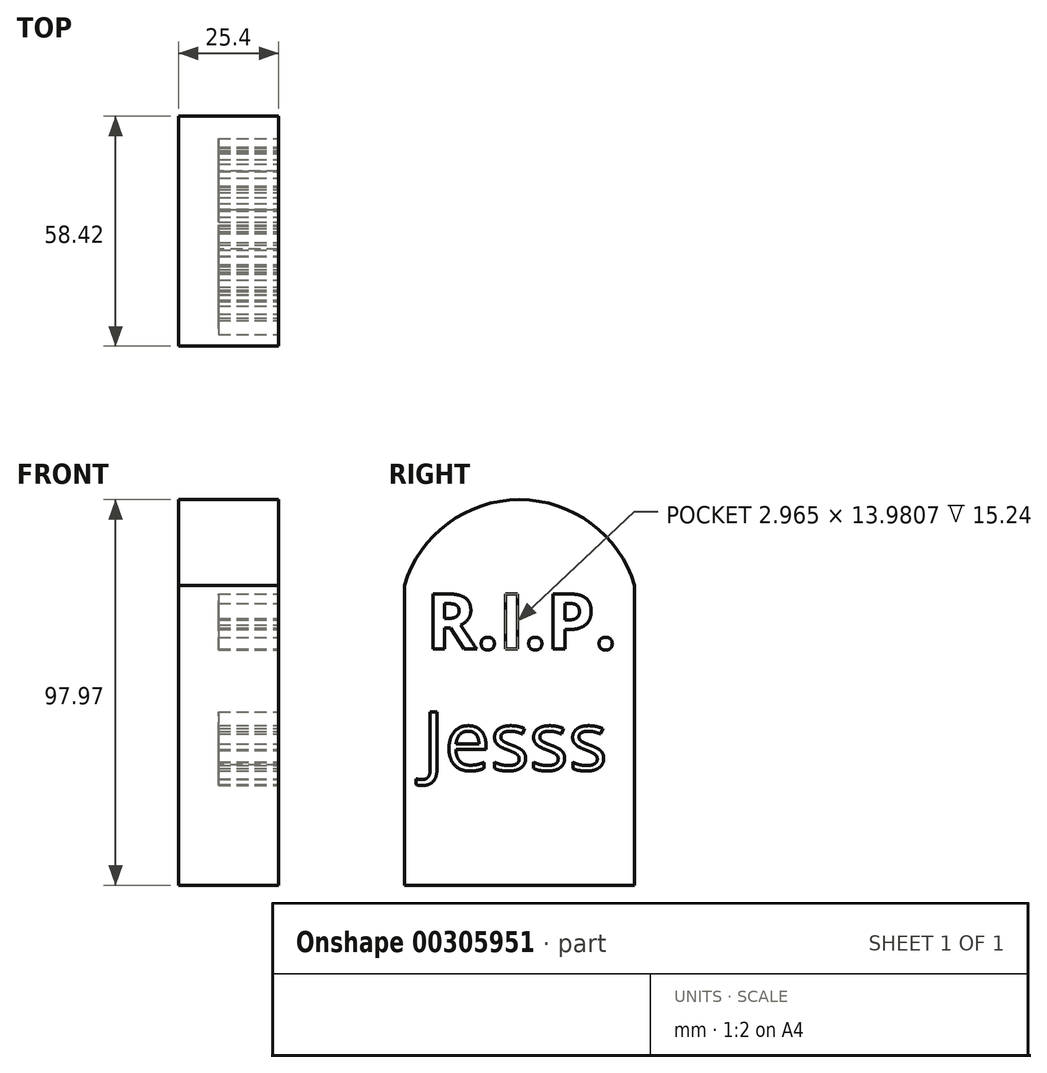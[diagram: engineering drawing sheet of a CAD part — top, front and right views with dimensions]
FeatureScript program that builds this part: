
annotation { "Feature Type Name" : "Feature", "Feature Type Description" : "" }
export const myFeature = defineFeature(function(context is Context, id is Id, definition is map)
    precondition{}
    {
        {
            var Q0;
            Q0=qCreatedBy(makeId("Right.planeOp"),FACE);
            var sketch = newSketch(context, id + "F0", { "sketchPlane" : qUnion([Q0])});
            skLineSegment(sketch, "E0.bottom", {"start": v(-17.8, -44.2) * mm, "end": v(40.62, -44.2) * mm});
            skLineSegment(sketch, "E0.top", {"start": v(-17.8, 32) * mm, "end": v(40.62, 32) * mm});
            skLineSegment(sketch, "E0.left", {"start": v(-17.8, -44.2) * mm, "end": v(-17.8, 32) * mm});
            skLineSegment(sketch, "E0.right", {"start": v(40.62, -44.2) * mm, "end": v(40.62, 32) * mm});
            skArc(sketch, "E1", {"start": v(40.62, 32) * mm, "mid": v(11.4, 53.78) * mm, "end": v(-17.8, 32) * mm});
            skSolve(sketch);
        }
        {
            var Q0;
            Q0=makeQuery(id+"F0.imprint","IMPRINT",FACE,{"disambiguationData":[TD([[makeQuery(id+"F0.imprint","IMPRINT",EDGE,{"derivedFrom":sQuery(id+"F0.wireOp",EDGE,"E0.bottom")}),1.0]])]});
            extrude(context, id + "F1", {"entities" : qUnion([Q0]), "depth" : 25.4 * mm});
        }
        {
            var Q0;
            Q0 = qSketchRegion(id + "F0", true);
            extrude(context, id + "F2", {"entities" : qUnion([Q0]), "operationType" : NewBodyOperationType.ADD, "depth" : 25.4 * mm});
        }
        {
            var Q0;
            {var subQ0=sQuery(id+"F0.wireOp",EDGE,"E0.right");var subQ1=sQuery(id+"F0.wireOp",EDGE,"E0.left");var subQ2=sQuery(id+"F0.wireOp",EDGE,"E0.bottom");Q0=makeQuery(id+"F2.boolean.opBoolean","MERGE",FACE,{"derivedFrom":[makeQuery(id+"F1.opExtrude","CAP_FACE",FACE,{"disambiguationData":[OSD([subQ2,sQuery(id+"F0.wireOp",EDGE,"E0.top"),subQ1,subQ0])],"isStart":false}),makeQuery(id+"F2.opExtrude","CAP_FACE",FACE,{"disambiguationData":[OSD([subQ2,subQ1,subQ0,sQuery(id+"F0.wireOp",EDGE,"E1")])],"isStart":false})]});}
            var sketch = newSketch(context, id + "F3", { "sketchPlane" : qUnion([Q0])});
            skText(sketch, "E2", { "text": "Jesss", "fontName": "OpenSans-Regular.ttf"});
            const initialGuessF3  = {"E2": [-0.01323, -0.01497, 1, 0, 0.01497]};
            skSetInitialGuess(sketch, initialGuessF3);
            skSolve(sketch);
        }
        {
            var Q0;
            Q0 = qSketchRegion(id + "F3", true);
            extrude(context, id + "F4", {"entities" : qUnion([Q0]), "operationType" : NewBodyOperationType.REMOVE, "oppositeDirection" : true, "depth" : 15.24 * mm});
        }
        {
            var Q0;
            {var subQ0=sQuery(id+"F0.wireOp",EDGE,"E0.right");var subQ1=sQuery(id+"F0.wireOp",EDGE,"E0.left");var subQ2=sQuery(id+"F0.wireOp",EDGE,"E0.bottom");var subQ3=sQuery(id+"F0.wireOp",EDGE,"E1");Q0=makeQuery(id+"F4.boolean.opBoolean","SPLIT",FACE,{"disambiguationData":[TD([makeQuery(id+"F1.opExtrude","SWEPT_FACE",FACE,{"disambiguationData":[OSD([subQ2])]})])],"derivedFrom":makeQuery(id+"F2.boolean.opBoolean","MERGE",FACE,{"derivedFrom":[makeQuery(id+"F1.opExtrude","CAP_FACE",FACE,{"disambiguationData":[OSD([subQ2,sQuery(id+"F0.wireOp",EDGE,"E0.top"),subQ1,subQ0])],"isStart":false}),makeQuery(id+"F2.opExtrude","CAP_FACE",FACE,{"disambiguationData":[OSD([subQ2,subQ1,subQ0,subQ3])],"isStart":false})]})});}
            var sketch = newSketch(context, id + "F5", { "sketchPlane" : qUnion([Q0])});
            skText(sketch, "E3", { "text": "R.I.P.", "fontName": "OpenSans-Bold.ttf"});
            const initialGuessF5  = {"E3": [-0.01238, 0.01583, 1, 0, 0.0141]};
            skSetInitialGuess(sketch, initialGuessF5);
            skSolve(sketch);
        }
        {
            var Q0;
            Q0 = qSketchRegion(id + "F5", true);
            extrude(context, id + "F6", {"entities" : qUnion([Q0]), "operationType" : NewBodyOperationType.REMOVE, "oppositeDirection" : true, "depth" : 15.24 * mm});
        }
        {
            var Q0;
            Q0=qCreatedBy(makeId("Right.planeOp"),FACE);
            var sketch = newSketch(context, id + "F7", { "sketchPlane" : qUnion([Q0])});
            skText(sketch, "E4", { "text": "2000-2016", "fontName": "OpenSans-Regular.ttf"});
            const initialGuessF7  = {"E4": [-0.01552, -0.03653, 1, 0, 0.0038]};
            skSetInitialGuess(sketch, initialGuessF7);
            skSolve(sketch);
        }
        {
            var Q0;
            Q0 = qSketchRegion(id + "F7", true);
            extrude(context, id + "F8", {"entities" : qUnion([Q0]), "operationType" : NewBodyOperationType.ADD, "depth" : 25.4 * mm});
        }
    });
